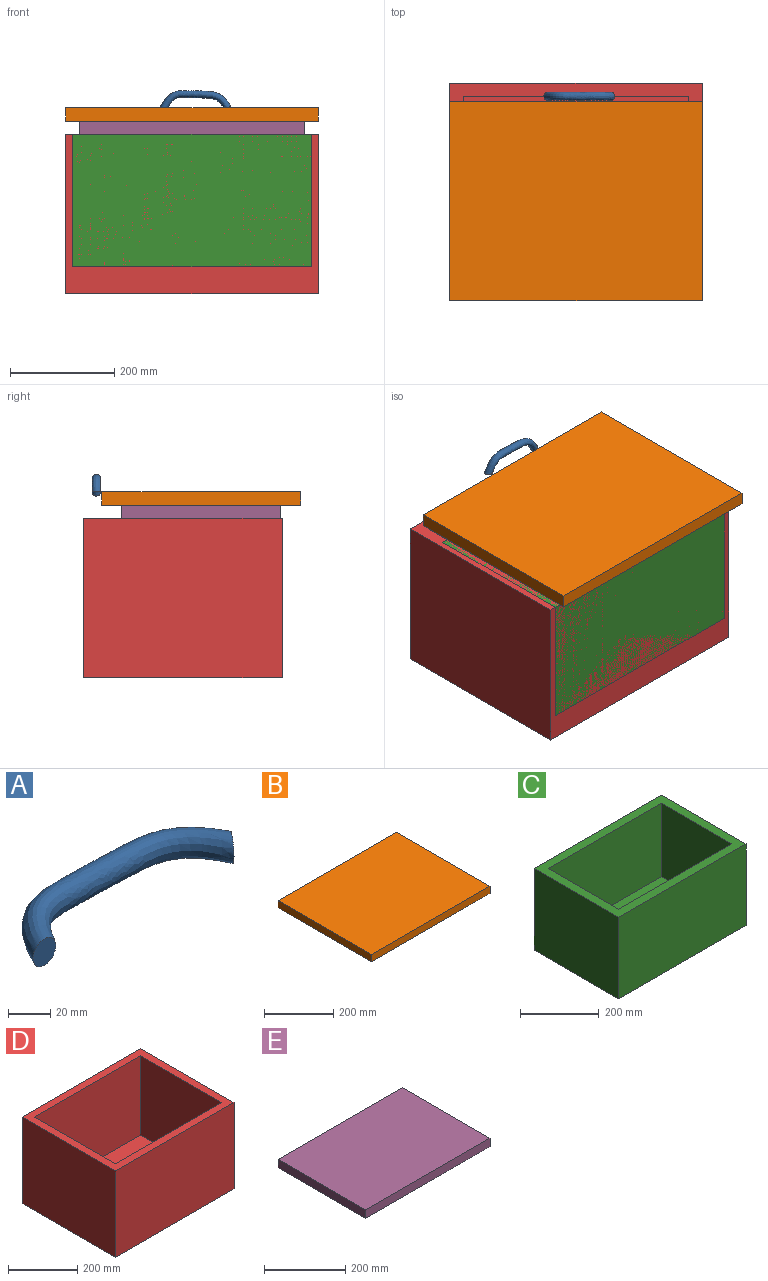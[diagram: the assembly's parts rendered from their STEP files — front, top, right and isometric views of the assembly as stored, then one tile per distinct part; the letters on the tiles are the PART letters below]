
ASSEMBLY  parts=5 mates=5
PART A: 3 faces, bbox 147.3x54.4x15.2 mm
  f0: plane 15.24x15.24mm, normal (0,-1,0), area 182.4mm2, adj f2
  f1: plane 15.24x12.12mm, normal (0.8,-0.61,0), area 182.4mm2, adj f2
  f2: bspline ~147.28x54.35mm, area 6619.3mm2, adj f0,f1
PART B: 6 faces, bbox 482.6x381x25.4 mm
  f0: plane 381x25.4mm, normal (-1,0,0), area 9677.4mm2, adj f1,f3,f4,f5
  f1: plane 482.6x25.4mm, normal (0,-1,0), area 12258mm2, adj f0,f2,f4,f5
  f2: plane 381x25.4mm, normal (1,0,0), area 9677.4mm2, adj f1,f3,f4,f5
  f3: plane 482.6x25.4mm, normal (0,1,0), area 12258mm2, adj f0,f2,f4,f5
  f4: plane 482.6x381mm, normal (0,0,1), area 183870.6mm2, adj f0,f1,f2,f3
  f5: plane 482.6x381mm, normal (0,0,-1), area 183870.6mm2, adj f0,f1,f2,f3
PART C: 11 faces, bbox 457.2x304.8x254 mm
  f0: plane 457.2x304.8mm, normal (0,0,1), area 36129mm2, adj f1,f2,f3,f4,f6,f7,f8,f9
  f1: plane 304.8x254mm, normal (-1,0,0), area 77419.2mm2, adj f0,f2,f4,f5
  f2: plane 457.2x254mm, normal (0,-1,0), area 116128.8mm2, adj f0,f1,f3,f5
  f3: plane 304.8x254mm, normal (1,0,0), area 77419.2mm2, adj f0,f2,f4,f5
  f4: plane 457.2x254mm, normal (0,1,0), area 116128.8mm2, adj f0,f1,f3,f5
  f5: plane 457.2x304.8mm, normal (0,0,-1), area 139354.6mm2, adj f1,f2,f3,f4
  f6: plane 254x228.6mm, normal (1,0,0), area 58064.4mm2, adj f0,f7,f9,f10
  f7: plane 406.4x228.6mm, normal (0,1,0), area 92903mm2, adj f0,f6,f8,f10
  f8: plane 254x228.6mm, normal (-1,0,0), area 58064.4mm2, adj f0,f7,f9,f10
  f9: plane 406.4x228.6mm, normal (0,-1,0), area 92903mm2, adj f0,f6,f8,f10
  f10: plane 406.4x254mm, normal (0,0,1), area 103225.6mm2, adj f6,f7,f8,f9
PART D: 11 faces, bbox 482.6x381x304.8 mm
  f0: plane 482.6x381mm, normal (0,0,1), area 41290.2mm2, adj f1,f2,f3,f4,f6,f7,f8,f9
  f1: plane 381x304.8mm, normal (-1,0,0), area 116128.8mm2, adj f0,f2,f4,f5
  f2: plane 482.6x304.8mm, normal (0,-1,0), area 147096.5mm2, adj f0,f1,f3,f5
  f3: plane 381x304.8mm, normal (1,0,0), area 116128.8mm2, adj f0,f2,f4,f5
  f4: plane 482.6x304.8mm, normal (0,1,0), area 147096.5mm2, adj f0,f1,f3,f5
  f5: plane 482.6x381mm, normal (0,0,-1), area 183870.6mm2, adj f1,f2,f3,f4
  f6: plane 330.2x279.4mm, normal (1,0,0), area 92257.9mm2, adj f0,f7,f9,f10
  f7: plane 431.8x279.4mm, normal (0,1,0), area 120644.9mm2, adj f0,f6,f8,f10
  f8: plane 330.2x279.4mm, normal (-1,0,0), area 92257.9mm2, adj f0,f7,f9,f10
  f9: plane 431.8x279.4mm, normal (0,-1,0), area 120644.9mm2, adj f0,f6,f8,f10
  f10: plane 431.8x330.2mm, normal (0,0,1), area 142580.4mm2, adj f6,f7,f8,f9
PART E: 6 faces, bbox 431.8x304.8x25.4 mm
  f0: plane 304.8x25.4mm, normal (-1,0,0), area 7741.9mm2, adj f1,f3,f4,f5
  f1: plane 431.8x25.4mm, normal (0,-1,0), area 10967.7mm2, adj f0,f2,f4,f5
  f2: plane 304.8x25.4mm, normal (1,0,0), area 7741.9mm2, adj f1,f3,f4,f5
  f3: plane 431.8x25.4mm, normal (0,1,0), area 10967.7mm2, adj f0,f2,f4,f5
  f4: plane 431.8x304.8mm, normal (0,0,1), area 131612.6mm2, adj f0,f1,f2,f3
  f5: plane 431.8x304.8mm, normal (0,0,-1), area 131612.6mm2, adj f0,f1,f2,f3
PLACE A rot(axis=(1,0,0),90deg) t=(0,200.91,756.92)mm
PLACE B t=(0,0,731.52)mm
PLACE C t=(0,-2.54,452.12)mm
PLACE D t=(0,35.56,401.32)mm
PLACE E t=(0,0,706.12)mm
MATE planar B.f5 <-> E.f4  axis (0,0,-1) through (0,0,731.52)mm
MATE fastened E.f4 <-> B.f5  axis (0,0,1) through (0,0,731.52)mm
MATE planar E.f5 <-> C.f0  axis (0,0,-1) through (0,0,706.12)mm
MATE planar C.f2 <-> D.f2  axis (0,-1,0) through (0,-154.94,579.12)mm
MATE planar E.f5 <-> D.f0  axis (0,0,-1) through (0,0,706.12)mm
